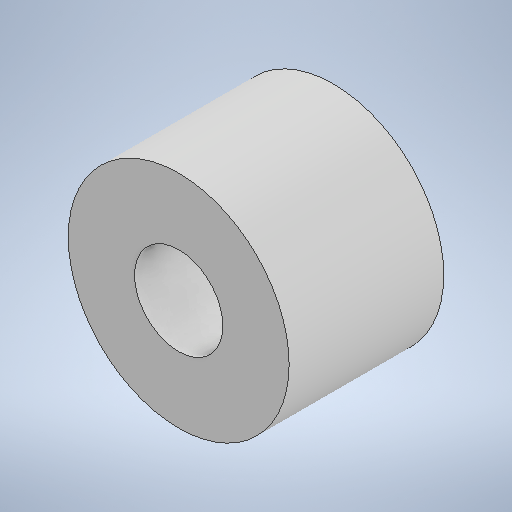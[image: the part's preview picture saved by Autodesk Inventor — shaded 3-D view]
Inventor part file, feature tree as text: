
AUTODESK INVENTOR PART (.ipt)
format: ipt  version: 2025.1 (Build 291241020, 241B)  size: 210,944 bytes
history: native  units: in
note: dims shown in document units (in); Inventor stores cm internally (conversion verified against a paired STEP export)
features: extrude x1, sketch x1
ambient origin geometry x8: Origin, YZ Plane, XZ Plane, XY Plane, X Axis, Y Axis, Z Axis, Center Point
bodies: Solid1 (feature_tree)
feature tree (2):
  extrude  "Extrusion1"  Depth=0.35in
  sketch  "Sketch1"  dims[d0=0.2in d1=0.5in d2=0.35in d3=0.0in]
